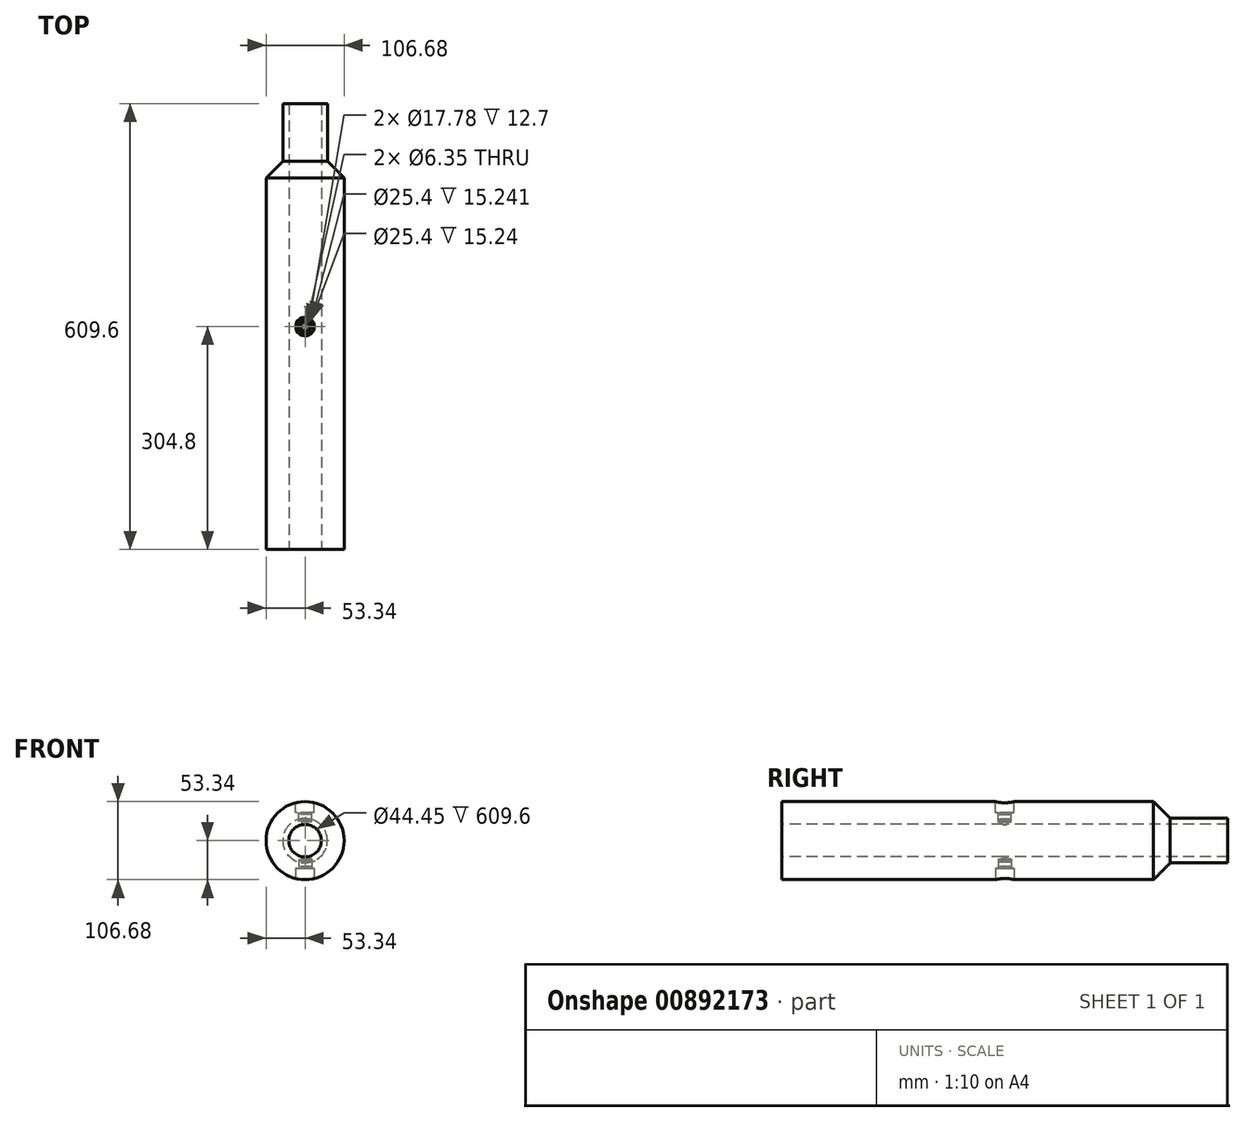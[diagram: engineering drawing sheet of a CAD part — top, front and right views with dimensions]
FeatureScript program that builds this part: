
annotation { "Feature Type Name" : "Feature", "Feature Type Description" : "" }
export const myFeature = defineFeature(function(context is Context, id is Id, definition is map)
    precondition{}
    {
        {
            var Q0;
            Q0=qCreatedBy(makeId("Front.planeOp"),FACE);
            var sketch = newSketch(context, id + "F0", { "sketchPlane" : qUnion([Q0])});
            skCircle(sketch, "E0", {"center": v(0, 0) * mm, "radius": 22.23 * mm});
            skCircle(sketch, "E1", {"center": v(0, 0) * mm, "radius": 53.34 * mm});
            skSolve(sketch);
        }
        {
            var Q0;
            Q0=makeQuery(id+"F0.imprint","IMPRINT",FACE,{"disambiguationData":[TD([[makeQuery(id+"F0.imprint","IMPRINT",EDGE,{"derivedFrom":sQuery(id+"F0.wireOp",EDGE,"E0")}),-1.0]])]});
            extrude(context, id + "F1", {"entities" : qUnion([Q0]), "endBound" : BoundingType.SYMMETRIC, "oppositeDirection" : true, "depth" : 609.6 * mm, "offsetDistance" : 25.4 * mm});
        }
        {
            var Q0;
            Q0=makeQuery(id+"F1.opExtrude","CAP_FACE",FACE,{"disambiguationData":[OSD([sQuery(id+"F0.wireOp",EDGE,"E0"),sQuery(id+"F0.wireOp",EDGE,"E1")])],"isStart":false});
            cPlane(context, id + "F2", {"entities" : qUnion([Q0]), "cplaneType" : CPlaneType.OFFSET, "offset" : 0 * mm, "oppositeDirection" : true, "width" : 152.4 * mm, "height" : 152.4 * mm});
        }
        {
            var Q0;
            Q0=qCreatedBy(makeId("Front.planeOp"),FACE);
            cPlane(context, id + "F3", {"entities" : qUnion([Q0]), "cplaneType" : CPlaneType.OFFSET, "offset" : 203.2 * mm, "oppositeDirection" : true, "width" : 152.4 * mm, "height" : 152.4 * mm});
        }
        {
            var Q0;
            Q0=qCreatedBy(id+"F2.planeOp",FACE);
            var sketch = newSketch(context, id + "F4", { "sketchPlane" : qUnion([Q0])});
            skCircle(sketch, "E2", {"center": v(0, 0) * mm, "radius": 22.23 * mm});
            skCircle(sketch, "E3", {"center": v(0, 0) * mm, "radius": 30.48 * mm});
            skCircle(sketch, "E4", {"center": v(0, 0) * mm, "radius": 53.34 * mm});
            skSolve(sketch);
        }
        {
            var Q0;
            Q0=makeQuery(id+"F4.imprint","IMPRINT",FACE,{"disambiguationData":[TD([[makeQuery(id+"F4.imprint","IMPRINT",EDGE,{"derivedFrom":sQuery(id+"F4.wireOp",EDGE,"E3")}),-1.0]])]});
            var Q1;
            Q1=qCreatedBy(id+"F3.planeOp",FACE);
            extrude(context, id + "F5", {"entities" : qUnion([Q0]), "operationType" : NewBodyOperationType.REMOVE, "oppositeDirection" : true, "depth" : 101.6 * mm, "endBoundEntityFace" : qUnion([Q1]), "offsetDistance" : 25.4 * mm});
        }
        {
            var Q0;
            Q0=qCreatedBy(makeId("Right.planeOp"),FACE);
            var sketch = newSketch(context, id + "F6", { "sketchPlane" : qUnion([Q0])});
            skLineSegment(sketch, "E5", {"start": v(0, 0) * mm, "end": v(203.2, 0) * mm, "construction": true});
            skLineSegment(sketch, "E6", {"start": v(203.2, 0) * mm, "end": v(203.2, 53.34) * mm});
            skLineSegment(sketch, "E7", {"start": v(203.2, 0) * mm, "end": v(203.2, 30.48) * mm});
            skLineSegment(sketch, "E8", {"start": v(203.2, 30.48) * mm, "end": v(226.06, 30.48) * mm});
            skLineSegment(sketch, "E9", {"start": v(226.06, 30.48) * mm, "end": v(203.2, 53.34) * mm});
            skSolve(sketch);
        }
        {
            var Q0;
            Q0=makeQuery(id+"F6.imprint","IMPRINT",FACE,{"disambiguationData":[TD([[makeQuery(id+"F6.imprint","IMPRINT",EDGE,{"derivedFrom":sQuery(id+"F6.wireOp",EDGE,"E6")}),-1.0]])]});
            var Q1;
            Q1=sQuery(id+"F6.wireOp",EDGE,"E5");
            revolve(context, id + "F7", {"operationType" : NewBodyOperationType.ADD, "surfaceOperationType" : NewSurfaceOperationType.NEW, "entities" : qUnion([Q0]), "axis" : qUnion([Q1]), "revolveType" : RevolveType.FULL});
        }
        {
            var Q0;
            Q0=qCreatedBy(makeId("Top.planeOp"),FACE);
            cPlane(context, id + "F8", {"entities" : qUnion([Q0]), "cplaneType" : CPlaneType.OFFSET, "offset" : 53.34 * mm, "width" : 152.4 * mm, "height" : 152.4 * mm});
        }
        {
            var Q0;
            Q0=qCreatedBy(makeId("Top.planeOp"),FACE);
            cPlane(context, id + "F9", {"entities" : qUnion([Q0]), "cplaneType" : CPlaneType.OFFSET, "offset" : 53.34 * mm, "oppositeDirection" : true, "width" : 152.4 * mm, "height" : 152.4 * mm});
        }
        {
            var Q0;
            Q0=qCreatedBy(id+"F8.planeOp",FACE);
            var sketch = newSketch(context, id + "F10", { "sketchPlane" : qUnion([Q0])});
            skCircle(sketch, "E10", {"center": v(0, 0) * mm, "radius": 12.7 * mm});
            skCircle(sketch, "E11", {"center": v(0, 0) * mm, "radius": 8.9 * mm});
            skCircle(sketch, "E12", {"center": v(0, 0) * mm, "radius": 3.18 * mm});
            skSolve(sketch);
        }
        {
            var Q0;
            Q0=makeQuery(id+"F10.imprint","IMPRINT",FACE,{"disambiguationData":[TD([[makeQuery(id+"F10.imprint","IMPRINT",EDGE,{"derivedFrom":sQuery(id+"F10.wireOp",EDGE,"E10")}),1.0]])]});
            var Q1;
            Q1=makeQuery(id+"F10.imprint","IMPRINT",FACE,{"disambiguationData":[TD([[makeQuery(id+"F10.imprint","IMPRINT",EDGE,{"derivedFrom":sQuery(id+"F10.wireOp",EDGE,"E12")}),1.0]])]});
            var Q2;
            Q2=makeQuery(id+"F10.imprint","IMPRINT",FACE,{"disambiguationData":[TD([[makeQuery(id+"F10.imprint","IMPRINT",EDGE,{"derivedFrom":sQuery(id+"F10.wireOp",EDGE,"E11")}),1.0]])]});
            extrude(context, id + "F11", {"entities" : qUnion([Q0, Q1, Q2]), "operationType" : NewBodyOperationType.REMOVE, "oppositeDirection" : true, "depth" : 15.24 * mm, "offsetDistance" : 25.4 * mm});
        }
        {
            var Q0;
            Q0=makeQuery(id+"F10.imprint","IMPRINT",FACE,{"disambiguationData":[TD([[makeQuery(id+"F10.imprint","IMPRINT",EDGE,{"derivedFrom":sQuery(id+"F10.wireOp",EDGE,"E11")}),1.0]])]});
            var Q1;
            Q1=makeQuery(id+"F10.imprint","IMPRINT",FACE,{"disambiguationData":[TD([[makeQuery(id+"F10.imprint","IMPRINT",EDGE,{"derivedFrom":sQuery(id+"F10.wireOp",EDGE,"E12")}),1.0]])]});
            extrude(context, id + "F12", {"entities" : qUnion([Q0, Q1]), "operationType" : NewBodyOperationType.REMOVE, "oppositeDirection" : true, "depth" : 27.94 * mm, "offsetDistance" : 25.4 * mm});
        }
        {
            var Q0;
            Q0=makeQuery(id+"F10.imprint","IMPRINT",FACE,{"disambiguationData":[TD([[makeQuery(id+"F10.imprint","IMPRINT",EDGE,{"derivedFrom":sQuery(id+"F10.wireOp",EDGE,"E12")}),1.0]])]});
            var Q1;
            Q1=makeQuery(id+"F1.opExtrude","SWEPT_FACE",FACE,{"disambiguationData":[OSD([sQuery(id+"F0.wireOp",EDGE,"E0")])]});
            extrude(context, id + "F13", {"entities" : qUnion([Q0]), "operationType" : NewBodyOperationType.REMOVE, "endBound" : BoundingType.UP_TO_SURFACE, "oppositeDirection" : true, "depth" : 53.34 * mm, "endBoundEntityFace" : qUnion([Q1]), "offsetDistance" : 25.4 * mm});
        }
        {
            var Q0;
            Q0=qCreatedBy(id+"F9.planeOp",FACE);
            var sketch = newSketch(context, id + "F14", { "sketchPlane" : qUnion([Q0])});
            skCircle(sketch, "E13", {"center": v(0, 0) * mm, "radius": 12.7 * mm});
            skCircle(sketch, "E14", {"center": v(0, 0) * mm, "radius": 8.9 * mm});
            skCircle(sketch, "E15", {"center": v(0, 0) * mm, "radius": 3.18 * mm});
            skSolve(sketch);
        }
        {
            var Q0;
            Q0=qSketchRegion(id+"F14",true);
            var Q1;
            Q1=makeQuery(id+"F14.imprint","IMPRINT",FACE,{"disambiguationData":[TD([[makeQuery(id+"F14.imprint","IMPRINT",EDGE,{"derivedFrom":sQuery(id+"F14.wireOp",EDGE,"E14")}),1.0]])]});
            var Q2;
            Q2=makeQuery(id+"F14.imprint","IMPRINT",FACE,{"disambiguationData":[TD([[makeQuery(id+"F14.imprint","IMPRINT",EDGE,{"derivedFrom":sQuery(id+"F14.wireOp",EDGE,"E15")}),1.0]])]});
            extrude(context, id + "F15", {"entities" : qUnion([Q0, Q1, Q2]), "operationType" : NewBodyOperationType.REMOVE, "depth" : 15.24 * mm, "offsetDistance" : 25.4 * mm});
        }
        {
            var Q0;
            Q0=makeQuery(id+"F14.imprint","IMPRINT",FACE,{"disambiguationData":[TD([[makeQuery(id+"F14.imprint","IMPRINT",EDGE,{"derivedFrom":sQuery(id+"F14.wireOp",EDGE,"E14")}),1.0]])]});
            var Q1;
            Q1=makeQuery(id+"F14.imprint","IMPRINT",FACE,{"disambiguationData":[TD([[makeQuery(id+"F14.imprint","IMPRINT",EDGE,{"derivedFrom":sQuery(id+"F14.wireOp",EDGE,"E15")}),1.0]])]});
            extrude(context, id + "F16", {"entities" : qUnion([Q0, Q1]), "operationType" : NewBodyOperationType.REMOVE, "depth" : 27.94 * mm, "offsetDistance" : 25.4 * mm});
        }
        {
            var Q0;
            Q0=makeQuery(id+"F14.imprint","IMPRINT",FACE,{"disambiguationData":[TD([[makeQuery(id+"F14.imprint","IMPRINT",EDGE,{"derivedFrom":sQuery(id+"F14.wireOp",EDGE,"E15")}),1.0]])]});
            var Q1;
            Q1=makeQuery(id+"F1.opExtrude","SWEPT_FACE",FACE,{"disambiguationData":[OSD([sQuery(id+"F0.wireOp",EDGE,"E0")])]});
            extrude(context, id + "F17", {"entities" : qUnion([Q0]), "operationType" : NewBodyOperationType.REMOVE, "endBound" : BoundingType.UP_TO_SURFACE, "depth" : 25.4 * mm, "endBoundEntityFace" : qUnion([Q1]), "offsetDistance" : 25.4 * mm});
        }
        {
            var Q0;
            Q0=qCreatedBy(makeId("Top.planeOp"),FACE);
            cPlane(context, id + "F18", {"entities" : qUnion([Q0]), "cplaneType" : CPlaneType.OFFSET, "offset" : 38.1 * mm, "width" : 152.4 * mm, "height" : 152.4 * mm});
        }
        {
            var Q0;
            Q0=qCreatedBy(makeId("Top.planeOp"),FACE);
            cPlane(context, id + "F19", {"entities" : qUnion([Q0]), "cplaneType" : CPlaneType.OFFSET, "offset" : 38.1 * mm, "oppositeDirection" : true, "width" : 152.4 * mm, "height" : 152.4 * mm});
        }
        {
            var Q0;
            Q0=qCreatedBy(id+"F18.planeOp",FACE);
            var sketch = newSketch(context, id + "F20", { "sketchPlane" : qUnion([Q0])});
            skCircle(sketch, "E16", {"center": v(0, 0) * mm, "radius": 8.9 * mm});
            skSolve(sketch);
        }
        {
            var Q0;
            Q0 = qSketchRegion(id + "F20", true);
            extrude(context, id + "F21", {"entities" : qUnion([Q0]), "oppositeDirection" : true, "depth" : 11.43 * mm, "offsetDistance" : 25.4 * mm});
        }
        {
            var Q0;
            Q0=makeQuery(id+"F21.opExtrude","CAP_FACE",FACE,{"disambiguationData":[OSD([sQuery(id+"F20.wireOp",EDGE,"E16")])],"isStart":true});
            var Q1;
            Q1=makeQuery(id+"F21.opExtrude","CAP_EDGE",EDGE,{"disambiguationData":[OSD([sQuery(id+"F20.wireOp",EDGE,"E16")])],"isStart":false});
            chamfer(context, id + "F22", {"entities" : qUnion([Q0, Q1]), "width" : 2.54 * mm, "tangentPropagation" : true});
        }
        {
            var Q0;
            Q0=qCreatedBy(id+"F19.planeOp",FACE);
            var sketch = newSketch(context, id + "F23", { "sketchPlane" : qUnion([Q0])});
            skCircle(sketch, "E17", {"center": v(0, 0) * mm, "radius": 8.9 * mm});
            skSolve(sketch);
        }
        {
            var Q0;
            Q0 = qSketchRegion(id + "F23", true);
            extrude(context, id + "F24", {"entities" : qUnion([Q0]), "depth" : 11.43 * mm, "offsetDistance" : 25.4 * mm});
        }
        {
            var Q0;
            Q0=makeQuery(id+"F24.opExtrude","CAP_FACE",FACE,{"disambiguationData":[OSD([sQuery(id+"F23.wireOp",EDGE,"E17")])],"isStart":true});
            var Q1;
            Q1=makeQuery(id+"F24.opExtrude","CAP_FACE",FACE,{"disambiguationData":[OSD([sQuery(id+"F23.wireOp",EDGE,"E17")])],"isStart":false});
            chamfer(context, id + "F25", {"entities" : qUnion([Q0, Q1]), "width" : 2.54 * mm, "tangentPropagation" : true});
        }
    });
